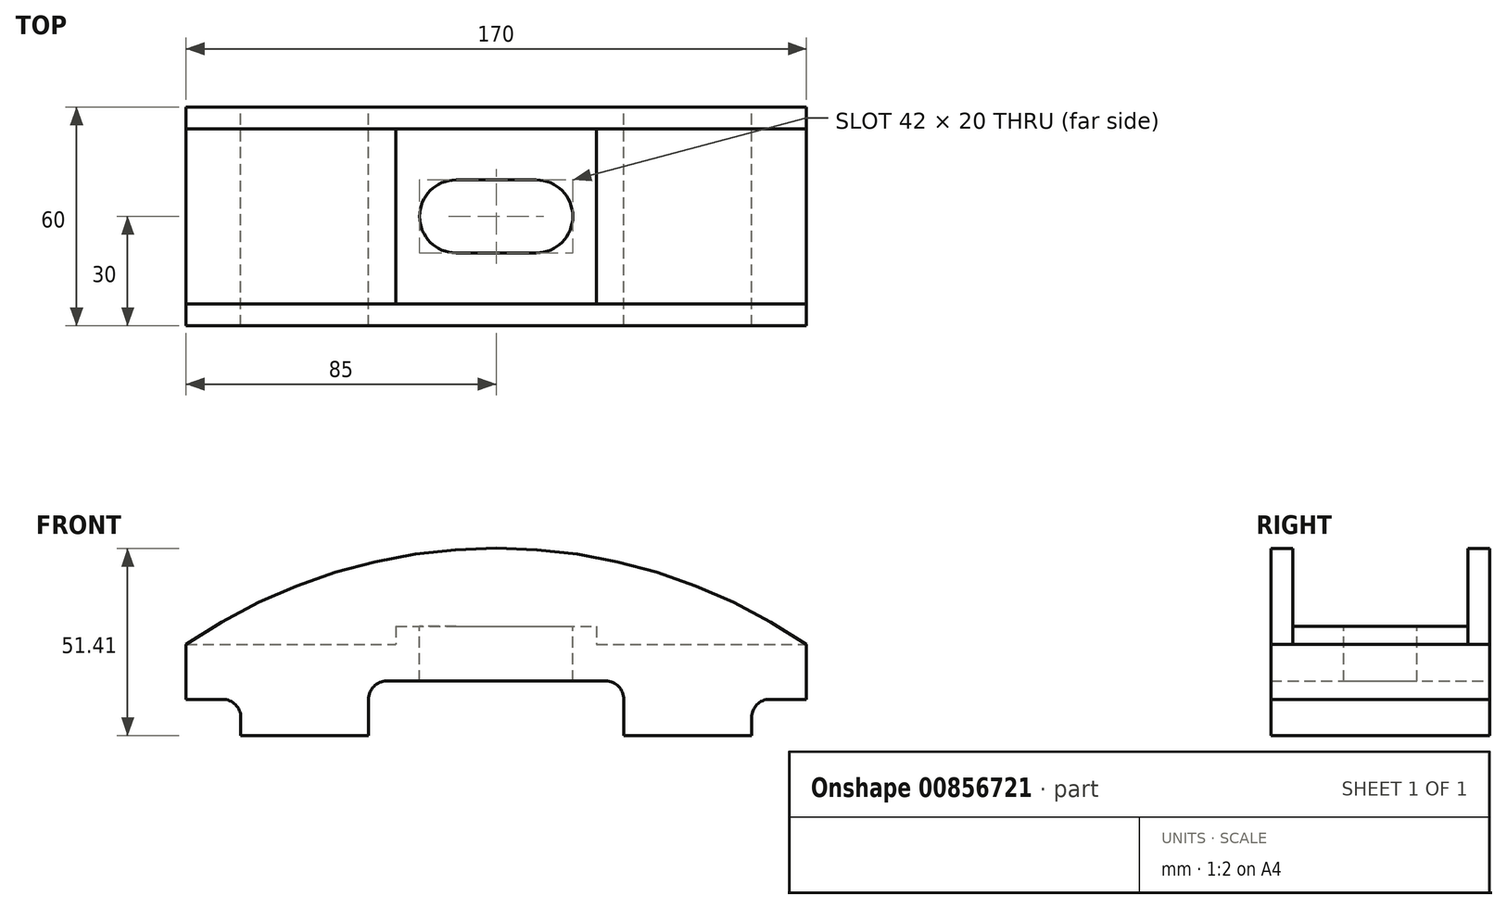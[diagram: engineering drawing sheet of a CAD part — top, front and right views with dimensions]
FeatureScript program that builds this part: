
annotation { "Feature Type Name" : "Feature", "Feature Type Description" : "" }
export const myFeature = defineFeature(function(context is Context, id is Id, definition is map)
    precondition{}
    {
        {
            var Q0;
            Q0=qCreatedBy(makeId("Front.planeOp"),FACE);
            var sketch = newSketch(context, id + "F0", { "sketchPlane" : qUnion([Q0])});
            skLineSegment(sketch, "E0.top", {"start": v(70, -30) * mm, "end": v(35, -30) * mm});
            skLineSegment(sketch, "E0.left", {"start": v(85, -5) * mm, "end": v(85, -20) * mm});
            skLineSegment(sketch, "E0.right", {"start": v(-85, -5) * mm, "end": v(-85, -20) * mm});
            skPoint(sketch, "E0.middle", {"position": v(0, 0) * mm});
            skLineSegment(sketch, "E1", {"start": v(-85, -20) * mm, "end": v(-85, -5) * mm});
            skLineSegment(sketch, "E2", {"start": v(85, -20) * mm, "end": v(85, -5) * mm});
            skArc(sketch, "E3", {"start": v(85, -5) * mm, "mid": v(0, 21.4) * mm, "end": v(-85, -5) * mm});
            skPoint(sketch, "E4.orphan", {"position": v(-85, 30) * mm});
            skPoint(sketch, "E5.orphan", {"position": v(85, 30) * mm});
            skLineSegment(sketch, "E6", {"start": v(-70, -30) * mm, "end": v(-70, -25) * mm});
            skLineSegment(sketch, "E7", {"start": v(70, -30) * mm, "end": v(70, -25) * mm});
            skLineSegment(sketch, "E8", {"start": v(-75, -20) * mm, "end": v(-85, -20) * mm});
            skLineSegment(sketch, "E9", {"start": v(75, -20) * mm, "end": v(85, -20) * mm});
            skPoint(sketch, "E10.orphan", {"position": v(-85, -30) * mm});
            skPoint(sketch, "E11.orphan", {"position": v(85, -30) * mm});
            skLineSegment(sketch, "E12", {"start": v(-35, -30) * mm, "end": v(-35, -20) * mm});
            skLineSegment(sketch, "E13", {"start": v(35, -30) * mm, "end": v(35, -20) * mm});
            skLineSegment(sketch, "E14", {"start": v(-30, -15) * mm, "end": v(30, -15) * mm});
            skPoint(sketch, "E15.start.orphan", {"position": v(0, -30) * mm});
            skLineSegment(sketch, "E16.trimOffspring", {"start": v(-35, -30) * mm, "end": v(-70, -30) * mm});
            skPoint(sketch, "E17.visualSharp", {"position": v(-35, -15) * mm});
            skArc(sketch, "E17.filletArc", {"start": v(-30, -15) * mm, "mid": v(-33.54, -16.46) * mm, "end": v(-35, -20) * mm});
            skPoint(sketch, "E18.visualSharp", {"position": v(35, -15) * mm});
            skArc(sketch, "E18.filletArc", {"start": v(35, -20) * mm, "mid": v(33.54, -16.46) * mm, "end": v(30, -15) * mm});
            skPoint(sketch, "E19.visualSharp", {"position": v(-70, -20) * mm});
            skArc(sketch, "E19.filletArc", {"start": v(-70, -25) * mm, "mid": v(-71.46, -21.46) * mm, "end": v(-75, -20) * mm});
            skPoint(sketch, "E20.visualSharp", {"position": v(70, -20) * mm});
            skArc(sketch, "E20.filletArc", {"start": v(75, -20) * mm, "mid": v(71.46, -21.46) * mm, "end": v(70, -25) * mm});
            skLineSegment(sketch, "E21", {"start": v(-85, -5) * mm, "end": v(85, -5) * mm});
            skSolve(sketch);
        }
        {
            var Q0;
            Q0=makeQuery(id+"F0.imprint","IMPRINT",FACE,{"disambiguationData":[TD([[makeQuery(id+"F0.imprint","IMPRINT",EDGE,{"derivedFrom":sQuery(id+"F0.wireOp",EDGE,"E0.top")}),-1.0]])]});
            extrude(context, id + "F1", {"entities" : qUnion([Q0]), "depth" : 60 * mm, "offsetDistance" : 25 * mm});
        }
        {
            var Q0;
            Q0=makeQuery(id+"F1.opExtrude","CAP_FACE",FACE,{"disambiguationData":[OSD([sQuery(id+"F0.wireOp",EDGE,"E0.top"),sQuery(id+"F0.wireOp",EDGE,"E1"),sQuery(id+"F0.wireOp",EDGE,"E2"),sQuery(id+"F0.wireOp",EDGE,"E6"),sQuery(id+"F0.wireOp",EDGE,"E7"),sQuery(id+"F0.wireOp",EDGE,"E8"),sQuery(id+"F0.wireOp",EDGE,"E9"),sQuery(id+"F0.wireOp",EDGE,"E12"),sQuery(id+"F0.wireOp",EDGE,"E13"),sQuery(id+"F0.wireOp",EDGE,"E14"),sQuery(id+"F0.wireOp",EDGE,"E16.trimOffspring"),sQuery(id+"F0.wireOp",EDGE,"E17.filletArc"),sQuery(id+"F0.wireOp",EDGE,"E18.filletArc"),sQuery(id+"F0.wireOp",EDGE,"E19.filletArc"),sQuery(id+"F0.wireOp",EDGE,"E20.filletArc"),sQuery(id+"F0.wireOp",EDGE,"E21")])],"isStart":true});
            var sketch = newSketch(context, id + "F2", { "sketchPlane" : qUnion([Q0])});
            skArc(sketch, "E22", {"start": v(85, -5) * mm, "mid": v(0, 21.4) * mm, "end": v(-85, -5) * mm});
            skSolve(sketch);
        }
        {
            var Q0;
            Q0=makeQuery(id+"F2.imprint","IMPRINT",FACE,{"disambiguationData":[TD([[makeQuery(id+"F2.imprint","IMPRINT",EDGE,{"derivedFrom":sQuery(id+"F2.wireOp",EDGE,"E22")}),1.0]])]});
            extrude(context, id + "F3", {"entities" : qUnion([Q0]), "operationType" : NewBodyOperationType.ADD, "oppositeDirection" : true, "depth" : 6 * mm, "offsetDistance" : 25 * mm});
        }
        {
            var Q0;
            Q0=makeQuery(id+"F1.opExtrude","CAP_FACE",FACE,{"disambiguationData":[OSD([sQuery(id+"F0.wireOp",EDGE,"E0.top"),sQuery(id+"F0.wireOp",EDGE,"E1"),sQuery(id+"F0.wireOp",EDGE,"E2"),sQuery(id+"F0.wireOp",EDGE,"E6"),sQuery(id+"F0.wireOp",EDGE,"E7"),sQuery(id+"F0.wireOp",EDGE,"E8"),sQuery(id+"F0.wireOp",EDGE,"E9"),sQuery(id+"F0.wireOp",EDGE,"E12"),sQuery(id+"F0.wireOp",EDGE,"E13"),sQuery(id+"F0.wireOp",EDGE,"E14"),sQuery(id+"F0.wireOp",EDGE,"E16.trimOffspring"),sQuery(id+"F0.wireOp",EDGE,"E17.filletArc"),sQuery(id+"F0.wireOp",EDGE,"E18.filletArc"),sQuery(id+"F0.wireOp",EDGE,"E19.filletArc"),sQuery(id+"F0.wireOp",EDGE,"E20.filletArc"),sQuery(id+"F0.wireOp",EDGE,"E21")])],"isStart":false});
            var sketch = newSketch(context, id + "F4", { "sketchPlane" : qUnion([Q0])});
            skArc(sketch, "E23", {"start": v(85, -5) * mm, "mid": v(0, 21.4) * mm, "end": v(-85, -5) * mm});
            skSolve(sketch);
        }
        {
            var Q0;
            Q0=makeQuery(id+"F4.imprint","IMPRINT",FACE,{"disambiguationData":[TD([[makeQuery(id+"F4.imprint","IMPRINT",EDGE,{"derivedFrom":sQuery(id+"F4.wireOp",EDGE,"E23")}),1.0]])]});
            extrude(context, id + "F5", {"entities" : qUnion([Q0]), "operationType" : NewBodyOperationType.ADD, "oppositeDirection" : true, "depth" : 6 * mm, "offsetDistance" : 25 * mm});
        }
        {
            var Q0;
            Q0=makeQuery(id+"F1.opExtrude","SWEPT_FACE",FACE,{"disambiguationData":[OSD([sQuery(id+"F0.wireOp",EDGE,"E21")])]});
            var sketch = newSketch(context, id + "F6", { "sketchPlane" : qUnion([Q0])});
            skLineSegment(sketch, "E24", {"start": v(0, 0) * mm, "end": v(0, -30) * mm});
            skPoint(sketch, "E24.endSnap0", {"position": v(0, -54) * mm});
            skLineSegment(sketch, "E25.bottom", {"start": v(27.5, -6) * mm, "end": v(-27.5, -6) * mm});
            skLineSegment(sketch, "E25.top", {"start": v(27.5, -54) * mm, "end": v(-27.5, -54) * mm});
            skLineSegment(sketch, "E25.left", {"start": v(27.5, -6) * mm, "end": v(27.5, -54) * mm});
            skLineSegment(sketch, "E25.right", {"start": v(-27.5, -6) * mm, "end": v(-27.5, -54) * mm});
            skPoint(sketch, "E25.middle", {"position": v(0, -30) * mm});
            skSolve(sketch);
        }
        {
            var Q0;
            Q0=makeQuery(id+"F6.imprint","IMPRINT",FACE,{"disambiguationData":[TD([[makeQuery(id+"F6.imprint","IMPRINT",EDGE,{"derivedFrom":sQuery(id+"F6.wireOp",EDGE,"E25.top")}),1.0]])]});
            extrude(context, id + "F7", {"entities" : qUnion([Q0]), "operationType" : NewBodyOperationType.ADD, "depth" : 5 * mm, "offsetDistance" : 25 * mm});
        }
        {
            var Q0;
            Q0=makeQuery(id+"F7.opExtrude","CAP_FACE",FACE,{"disambiguationData":[OSD([sQuery(id+"F6.wireOp",EDGE,"E25.bottom"),sQuery(id+"F6.wireOp",EDGE,"E25.top"),sQuery(id+"F6.wireOp",EDGE,"E25.left"),sQuery(id+"F6.wireOp",EDGE,"E25.right")])],"isStart":false});
            var sketch = newSketch(context, id + "F8", { "sketchPlane" : qUnion([Q0])});
            skLineSegment(sketch, "E26", {"start": v(0, -6) * mm, "end": v(0, -54) * mm});
            skLineSegment(sketch, "E27", {"start": v(0, -6) * mm, "end": v(0, -30) * mm});
            skLineSegment(sketch, "E28", {"start": v(0, -30) * mm, "end": v(11, -30) * mm});
            skLineSegment(sketch, "E29", {"start": v(0, -30) * mm, "end": v(-11, -30) * mm});
            skCircle(sketch, "E30", {"center": v(11, -30) * mm, "radius": 10 * mm});
            skCircle(sketch, "E31", {"center": v(-11, -30) * mm, "radius": 10 * mm});
            skLineSegment(sketch, "E32", {"start": v(-11, -30) * mm, "end": v(-11, -20) * mm});
            skLineSegment(sketch, "E33", {"start": v(-11, -30) * mm, "end": v(-11, -40) * mm});
            skLineSegment(sketch, "E34", {"start": v(11, -30) * mm, "end": v(11, -20) * mm});
            skLineSegment(sketch, "E35", {"start": v(11, -30) * mm, "end": v(11, -40) * mm});
            skLineSegment(sketch, "E36", {"start": v(-11, -20) * mm, "end": v(11, -20) * mm});
            skLineSegment(sketch, "E37", {"start": v(-11, -40) * mm, "end": v(11, -40) * mm});
            skSolve(sketch);
        }
        {
            var Q0;
            Q0 = qSketchRegion(id + "F8", true);
            extrude(context, id + "F9", {"entities" : qUnion([Q0]), "operationType" : NewBodyOperationType.REMOVE, "endBound" : BoundingType.THROUGH_ALL, "oppositeDirection" : true, "depth" : 25 * mm, "offsetDistance" : 25 * mm});
        }
    });
